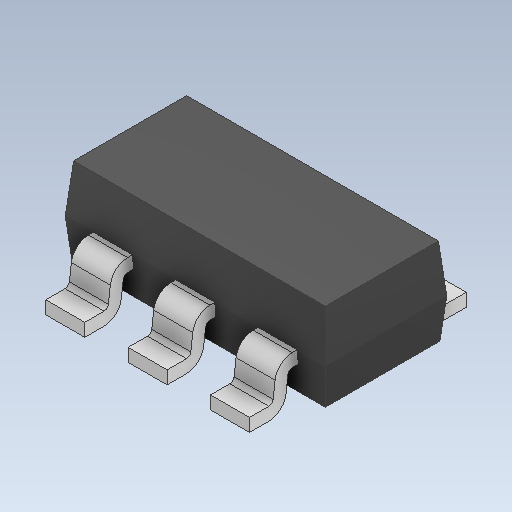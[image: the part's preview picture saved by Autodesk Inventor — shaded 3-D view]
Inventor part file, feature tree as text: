
AUTODESK INVENTOR PART (.ipt)
format: ipt  version: 2020 (Build 240168000, 168)  size: 158,720 bytes
history: native  units: mm
features: other x1, fillet x1
ambient origin geometry x8: Origin, YZ Plane, XZ Plane, XY Plane, X Axis, Y Axis, Z Axis, Center Point
bodies: Body1 (feature_tree)
feature tree (2):
  other  "Твердое тело1"
  fillet  "Fillet2"  [1 undecoded]
note: 1 required parameter value undecoded (feature->parameter linkage not recoverable at this tier; creation-order binding heuristic only, values carry confidence <= 0.55)
